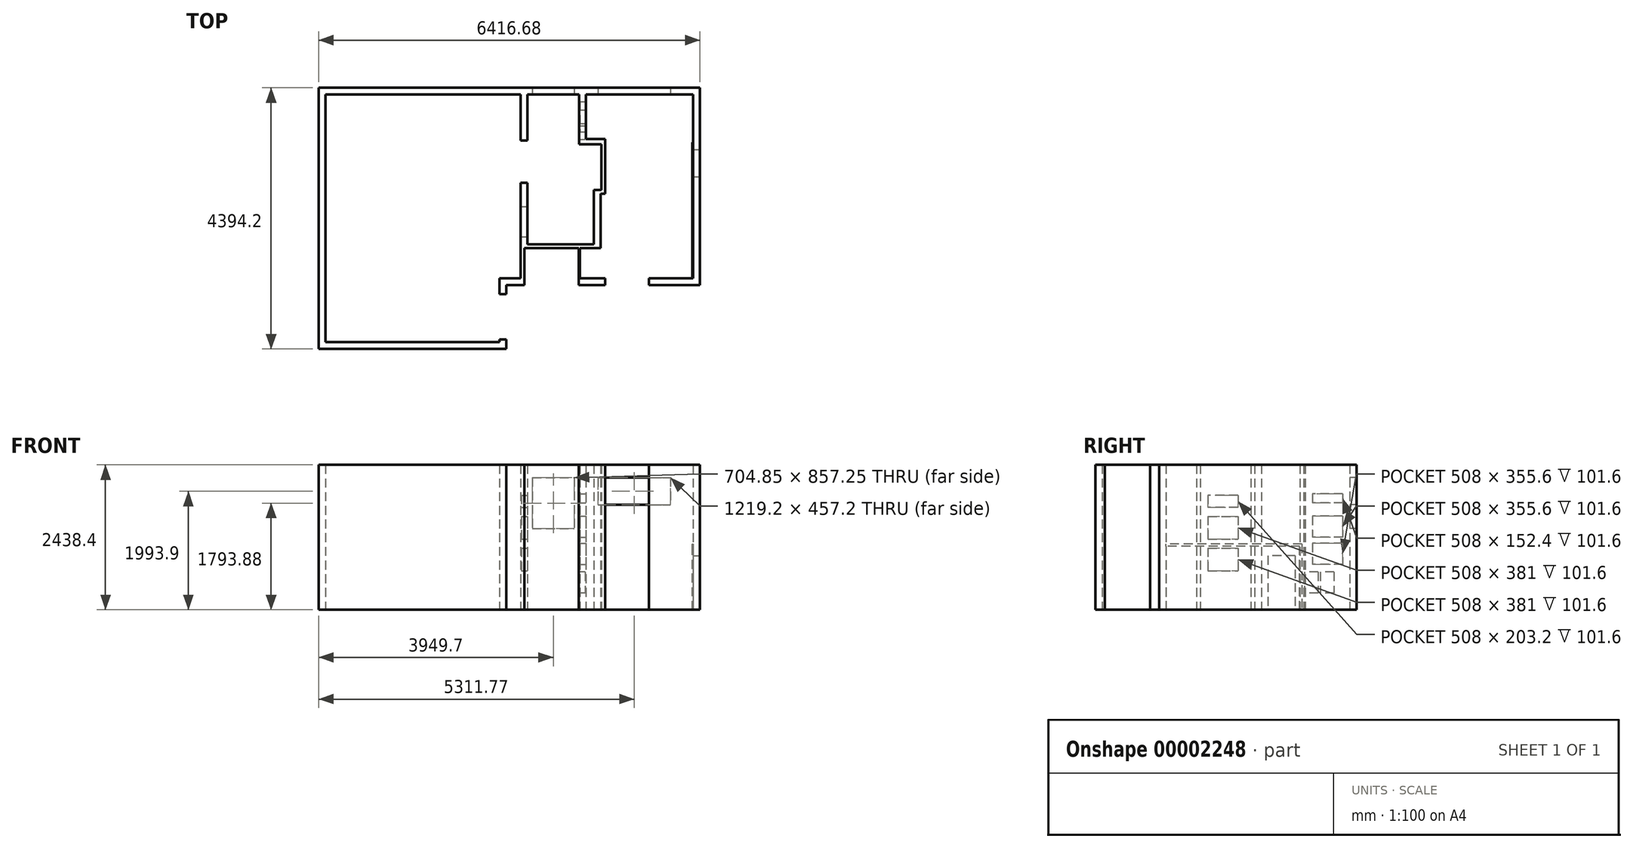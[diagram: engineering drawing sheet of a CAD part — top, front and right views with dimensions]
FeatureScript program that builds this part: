
annotation { "Feature Type Name" : "Feature", "Feature Type Description" : "" }
export const myFeature = defineFeature(function(context is Context, id is Id, definition is map)
    precondition{}
    {
        {
            var Q0;
            Q0=qCreatedBy(makeId("Top.planeOp"),FACE);
            var sketch = newSketch(context, id + "F0", { "sketchPlane" : qUnion([Q0])});
            skLineSegment(sketch, "E0.bottom", {"start": v(0, 0) * mm, "end": v(3286.13, 0) * mm});
            skLineSegment(sketch, "E0.top", {"start": v(0, -4165.6) * mm, "end": v(2930.53, -4165.6) * mm});
            skLineSegment(sketch, "E0.left", {"start": v(0, -4165.6) * mm, "end": v(0, 0) * mm});
            skLineSegment(sketch, "E0.right", {"start": v(2930.53, -3359.15) * mm, "end": v(2930.53, -3092.45) * mm});
            skLineSegment(sketch, "E1.bottom", {"start": v(2930.53, -3092.45) * mm, "end": v(3832.23, -3092.45) * mm});
            skLineSegment(sketch, "E1.right", {"start": v(3832.23, -3092.45) * mm, "end": v(3832.23, -1892.3) * mm});
            skLineSegment(sketch, "E2.top", {"start": v(3286.13, -1892.3) * mm, "end": v(3832.23, -1892.3) * mm});
            skLineSegment(sketch, "E2.right", {"start": v(3286.13, 0) * mm, "end": v(3286.13, -774.7) * mm});
            skLineSegment(sketch, "E3.0", {"start": v(-114.3, -4279.9) * mm, "end": v(3044.83, -4279.9) * mm});
            skLineSegment(sketch, "E3.1", {"start": v(-114.3, -4279.9) * mm, "end": v(-114.3, 114.3) * mm});
            skLineSegment(sketch, "E3.2", {"start": v(-114.3, 114.3) * mm, "end": v(3400.43, 114.3) * mm});
            skLineSegment(sketch, "E3.3", {"start": v(3400.43, 0) * mm, "end": v(3400.43, -774.7) * mm});
            skLineSegment(sketch, "E3.4", {"start": v(3400.43, -1778) * mm, "end": v(4422.78, -1778) * mm});
            skLineSegment(sketch, "E3.5", {"start": v(3044.83, -4279.9) * mm, "end": v(3044.83, -4121.15) * mm});
            skLineSegment(sketch, "E3.6", {"start": v(3946.53, -3092.45) * mm, "end": v(3946.53, -1892.3) * mm});
            skLineSegment(sketch, "E3.7", {"start": v(3044.83, -3206.75) * mm, "end": v(4594.23, -3206.75) * mm});
            skLineSegment(sketch, "E4", {"start": v(3400.43, 0) * mm, "end": v(4422.78, 0) * mm});
            skLineSegment(sketch, "E5", {"start": v(4422.78, 0) * mm, "end": v(4422.78, -1778) * mm});
            skLineSegment(sketch, "E6.0", {"start": v(4537.08, 0) * mm, "end": v(4537.08, -1892.3) * mm});
            skLineSegment(sketch, "E6.1", {"start": v(3400.43, 114.3) * mm, "end": v(4537.08, 114.3) * mm});
            skLineSegment(sketch, "E7.trimOffspring", {"start": v(3946.53, -1892.3) * mm, "end": v(4537.08, -1892.3) * mm});
            skLineSegment(sketch, "E8", {"start": v(4537.08, 114.3) * mm, "end": v(6302.38, 114.3) * mm});
            skLineSegment(sketch, "E9", {"start": v(6188.08, 0) * mm, "end": v(6188.08, -787.4) * mm});
            skLineSegment(sketch, "E10", {"start": v(6188.08, -787.4) * mm, "end": v(5400.68, -787.4) * mm});
            skLineSegment(sketch, "E11", {"start": v(5400.68, -787.4) * mm, "end": v(5400.68, -901.7) * mm});
            skLineSegment(sketch, "E12", {"start": v(5400.68, -901.7) * mm, "end": v(6188.08, -901.7) * mm});
            skLineSegment(sketch, "E13", {"start": v(6188.08, -901.7) * mm, "end": v(6188.08, -3092.45) * mm});
            skLineSegment(sketch, "E14", {"start": v(6302.38, -3206.75) * mm, "end": v(6302.38, 114.3) * mm});
            skLineSegment(sketch, "E15.trimOffspring", {"start": v(3946.53, -3092.45) * mm, "end": v(4594.23, -3092.45) * mm});
            skLineSegment(sketch, "E16.trimOffspring", {"start": v(4537.08, 0) * mm, "end": v(6188.08, 0) * mm});
            skLineSegment(sketch, "E17", {"start": v(3286.12, -774.7) * mm, "end": v(3400.43, -774.7) * mm});
            skLineSegment(sketch, "E18", {"start": v(3286.13, -1485.9) * mm, "end": v(3400.43, -1485.9) * mm});
            skLineSegment(sketch, "E19", {"start": v(4594.23, -3092.45) * mm, "end": v(4594.23, -3206.75) * mm});
            skLineSegment(sketch, "E20", {"start": v(5305.43, -3092.45) * mm, "end": v(5305.43, -3206.75) * mm});
            skLineSegment(sketch, "E21.trimOffspring", {"start": v(5305.43, -3092.45) * mm, "end": v(6188.08, -3092.45) * mm});
            skLineSegment(sketch, "E22.trimOffspring", {"start": v(5305.43, -3206.75) * mm, "end": v(6302.38, -3206.75) * mm});
            skLineSegment(sketch, "E23.trimOffspring", {"start": v(3286.13, -1485.9) * mm, "end": v(3286.13, -1892.3) * mm});
            skLineSegment(sketch, "E24.trimOffspring", {"start": v(3400.43, -1485.9) * mm, "end": v(3400.43, -1778) * mm});
            skLineSegment(sketch, "E25", {"start": v(2930.53, -3359.15) * mm, "end": v(3044.83, -3359.15) * mm});
            skLineSegment(sketch, "E26", {"start": v(2930.53, -4121.15) * mm, "end": v(3044.83, -4121.15) * mm});
            skLineSegment(sketch, "E27.trimOffspring", {"start": v(2930.53, -4121.15) * mm, "end": v(2930.53, -4165.6) * mm});
            skLineSegment(sketch, "E28.trimOffspring", {"start": v(3044.83, -3359.15) * mm, "end": v(3044.83, -3206.75) * mm});
            skSolve(sketch);
        }
        {
            var Q0;
            Q0=qCreatedBy(makeId("Top.planeOp"),FACE);
            var sketch = newSketch(context, id + "F1", { "sketchPlane" : qUnion([Q0])});
            skLineSegment(sketch, "E29.0", {"start": v(0, 0) * mm, "end": v(3286.13, 0) * mm});
            skLineSegment(sketch, "E29.1", {"start": v(0, -4165.6) * mm, "end": v(2930.53, -4165.6) * mm});
            skLineSegment(sketch, "E29.2", {"start": v(0, -4165.6) * mm, "end": v(0, 0) * mm});
            skLineSegment(sketch, "E29.3", {"start": v(2930.53, -3359.15) * mm, "end": v(2930.53, -3092.45) * mm});
            skLineSegment(sketch, "E29.4", {"start": v(2930.53, -3092.45) * mm, "end": v(3286.13, -3092.45) * mm});
            skLineSegment(sketch, "E29.7", {"start": v(3286.13, 0) * mm, "end": v(3286.13, -774.7) * mm});
            skLineSegment(sketch, "E29.8", {"start": v(-114.3, -4279.9) * mm, "end": v(3044.83, -4279.9) * mm});
            skLineSegment(sketch, "E29.9", {"start": v(-114.3, -4279.9) * mm, "end": v(-114.3, 114.3) * mm});
            skLineSegment(sketch, "E29.10", {"start": v(-114.3, 114.3) * mm, "end": v(3400.43, 114.3) * mm});
            skLineSegment(sketch, "E29.11", {"start": v(3400.43, 0) * mm, "end": v(3400.43, -774.7) * mm});
            skLineSegment(sketch, "E29.13", {"start": v(3044.83, -4279.9) * mm, "end": v(3044.83, -4121.15) * mm});
            skLineSegment(sketch, "E29.15", {"start": v(3044.83, -3206.75) * mm, "end": v(3349.63, -3206.75) * mm});
            skLineSegment(sketch, "E29.16", {"start": v(3400.43, 0) * mm, "end": v(4270.38, 0) * mm});
            skLineSegment(sketch, "E29.19", {"start": v(3400.43, 114.3) * mm, "end": v(4537.08, 114.3) * mm});
            skLineSegment(sketch, "E29.21", {"start": v(4537.08, 114.3) * mm, "end": v(6302.38, 114.3) * mm});
            skLineSegment(sketch, "E29.22", {"start": v(6188.08, 0) * mm, "end": v(6188.08, -917.58) * mm});
            skLineSegment(sketch, "E29.27", {"start": v(6302.38, -3206.75) * mm, "end": v(6302.38, 114.3) * mm});
            skLineSegment(sketch, "E29.29", {"start": v(4384.68, 0) * mm, "end": v(6188.08, 0) * mm});
            skLineSegment(sketch, "E29.30", {"start": v(3286.12, -774.7) * mm, "end": v(3400.43, -774.7) * mm});
            skLineSegment(sketch, "E29.31", {"start": v(3286.13, -1485.9) * mm, "end": v(3400.43, -1485.9) * mm});
            skLineSegment(sketch, "E29.34", {"start": v(5445.13, -3092.45) * mm, "end": v(6188.08, -3092.45) * mm});
            skLineSegment(sketch, "E29.35", {"start": v(5445.13, -3206.75) * mm, "end": v(6302.38, -3206.75) * mm});
            skLineSegment(sketch, "E29.36", {"start": v(3286.13, -1485.9) * mm, "end": v(3286.13, -1892.3) * mm});
            skLineSegment(sketch, "E29.37", {"start": v(3400.43, -1485.9) * mm, "end": v(3400.43, -1778) * mm});
            skLineSegment(sketch, "E29.38", {"start": v(2930.53, -3359.15) * mm, "end": v(3044.83, -3359.15) * mm});
            skLineSegment(sketch, "E29.39", {"start": v(2930.53, -4121.15) * mm, "end": v(3044.83, -4121.15) * mm});
            skLineSegment(sketch, "E29.40", {"start": v(2930.53, -4121.15) * mm, "end": v(2930.53, -4165.6) * mm});
            skLineSegment(sketch, "E29.41", {"start": v(3044.83, -3359.15) * mm, "end": v(3044.83, -3206.75) * mm});
            skLineSegment(sketch, "E30", {"start": v(3286.13, -1892.3) * mm, "end": v(3286.13, -3092.45) * mm});
            skPoint(sketch, "E31.start.orphan", {"position": v(3400.43, -1778) * mm});
            skLineSegment(sketch, "E32", {"start": v(3400.43, -1778) * mm, "end": v(3400.43, -2517.78) * mm});
            skLineSegment(sketch, "E33", {"start": v(4384.68, 0) * mm, "end": v(4384.68, -749.3) * mm});
            skLineSegment(sketch, "E34", {"start": v(4384.68, -749.3) * mm, "end": v(4708.53, -749.3) * mm});
            skLineSegment(sketch, "E35", {"start": v(4708.53, -749.3) * mm, "end": v(4708.53, -1666.87) * mm});
            skLineSegment(sketch, "E36.0", {"start": v(4645.03, -838.2) * mm, "end": v(4645.03, -1603.37) * mm});
            skLineSegment(sketch, "E36.1", {"start": v(4270.38, -838.2) * mm, "end": v(4645.03, -838.2) * mm});
            skLineSegment(sketch, "E36.2", {"start": v(4270.38, 0) * mm, "end": v(4270.38, -838.2) * mm});
            skLineSegment(sketch, "E37", {"start": v(5445.13, -3092.45) * mm, "end": v(5445.13, -3206.75) * mm});
            skLineSegment(sketch, "E38", {"start": v(4708.53, -3092.45) * mm, "end": v(4708.53, -3206.75) * mm});
            skLineSegment(sketch, "E39.bottom", {"start": v(5654.68, -1543.05) * mm, "end": v(6188.08, -1543.05) * mm, "construction": true});
            skLineSegment(sketch, "E39.left", {"start": v(5654.68, -1543.05) * mm, "end": v(5654.68, -3092.45) * mm, "construction": true});
            skLineSegment(sketch, "E39.right", {"start": v(6188.08, -1543.05) * mm, "end": v(6188.08, -2711.45) * mm, "construction": true});
            skLineSegment(sketch, "E40.bottom", {"start": v(4384.68, 0) * mm, "end": v(6188.08, 0) * mm, "construction": true});
            skLineSegment(sketch, "E40.top", {"start": v(4384.68, -749.3) * mm, "end": v(6188.08, -749.3) * mm, "construction": true});
            skLineSegment(sketch, "E40.left", {"start": v(4384.68, 0) * mm, "end": v(4384.68, -749.3) * mm, "construction": true});
            skLineSegment(sketch, "E40.right", {"start": v(6188.08, 0) * mm, "end": v(6188.08, -749.3) * mm, "construction": true});
            skLineSegment(sketch, "E41.0", {"start": v(4587.88, -647.7) * mm, "end": v(5984.88, -647.7) * mm, "construction": true});
            skLineSegment(sketch, "E41.1", {"start": v(4486.28, -203.2) * mm, "end": v(4486.28, -546.1) * mm, "construction": true});
            skLineSegment(sketch, "E41.2", {"start": v(4587.88, -101.6) * mm, "end": v(5984.88, -101.6) * mm, "construction": true});
            skLineSegment(sketch, "E41.3", {"start": v(6086.48, -203.2) * mm, "end": v(6086.48, -546.1) * mm, "construction": true});
            skPoint(sketch, "E42.visualSharp", {"position": v(4486.28, -101.6) * mm});
            skArc(sketch, "E42.filletArc", {"start": v(4587.88, -101.6) * mm, "mid": v(4516.03, -131.36) * mm, "end": v(4486.28, -203.2) * mm, "construction": true});
            skPoint(sketch, "E43.visualSharp", {"position": v(4486.28, -647.7) * mm});
            skArc(sketch, "E43.filletArc", {"start": v(4486.28, -546.1) * mm, "mid": v(4516.03, -617.94) * mm, "end": v(4587.88, -647.7) * mm, "construction": true});
            skPoint(sketch, "E44.visualSharp", {"position": v(6086.48, -647.7) * mm});
            skArc(sketch, "E44.filletArc", {"start": v(5984.88, -647.7) * mm, "mid": v(6056.72, -617.94) * mm, "end": v(6086.48, -546.1) * mm, "construction": true});
            skPoint(sketch, "E45.visualSharp", {"position": v(6086.48, -101.6) * mm});
            skArc(sketch, "E45.filletArc", {"start": v(6086.48, -203.2) * mm, "mid": v(6056.72, -131.36) * mm, "end": v(5984.88, -101.6) * mm, "construction": true});
            skLineSegment(sketch, "E46", {"start": v(3400.43, -2517.78) * mm, "end": v(4518.03, -2517.78) * mm});
            skLineSegment(sketch, "E47", {"start": v(3349.63, -3092.45) * mm, "end": v(3349.63, -3206.75) * mm});
            skLineSegment(sketch, "E48.trimOffspring", {"start": v(3349.63, -2581.27) * mm, "end": v(4264.03, -2581.27) * mm});
            skLineSegment(sketch, "E49", {"start": v(3400.43, -1603.37) * mm, "end": v(4645.03, -1603.37) * mm, "construction": true});
            skLineSegment(sketch, "E50", {"start": v(3349.63, -2581.27) * mm, "end": v(3349.63, -3092.45) * mm});
            skLineSegment(sketch, "E51", {"start": v(4264.03, -2581.27) * mm, "end": v(4264.03, -3206.75) * mm});
            skLineSegment(sketch, "E52", {"start": v(4283.08, -2581.27) * mm, "end": v(4283.08, -3092.45) * mm});
            skLineSegment(sketch, "E53.trimOffspring", {"start": v(4283.08, -3092.45) * mm, "end": v(4708.53, -3092.45) * mm});
            skLineSegment(sketch, "E54.trimOffspring", {"start": v(4264.03, -3206.75) * mm, "end": v(4708.53, -3206.75) * mm});
            skLineSegment(sketch, "E55", {"start": v(4111.63, -838.2) * mm, "end": v(4111.63, -1603.37) * mm, "construction": true});
            skLineSegment(sketch, "E56", {"start": v(4111.63, -838.2) * mm, "end": v(4270.38, -838.2) * mm, "construction": true});
            skLineSegment(sketch, "E57.trimOffspring", {"start": v(4283.08, -2581.27) * mm, "end": v(4632.33, -2581.27) * mm});
            skLineSegment(sketch, "E58.bottom", {"start": v(5816.21, -1708.15) * mm, "end": v(5968.61, -1708.15) * mm, "construction": true});
            skLineSegment(sketch, "E58.top", {"start": v(5816.21, -2012.95) * mm, "end": v(5968.61, -2012.95) * mm, "construction": true});
            skLineSegment(sketch, "E58.left", {"start": v(5765.41, -1758.95) * mm, "end": v(5765.41, -1962.15) * mm, "construction": true});
            skLineSegment(sketch, "E58.right", {"start": v(6019.41, -1758.95) * mm, "end": v(6019.41, -1962.15) * mm, "construction": true});
            skLineSegment(sketch, "E59", {"start": v(5654.68, -2317.75) * mm, "end": v(5806.28, -2317.75) * mm, "construction": true});
            skPoint(sketch, "E60.visualSharp", {"position": v(5765.41, -1708.15) * mm});
            skArc(sketch, "E60.filletArc", {"start": v(5816.21, -1708.15) * mm, "mid": v(5780.3, -1723.03) * mm, "end": v(5765.41, -1758.95) * mm, "construction": true});
            skPoint(sketch, "E61.visualSharp", {"position": v(6019.41, -1708.15) * mm});
            skArc(sketch, "E61.filletArc", {"start": v(6019.41, -1758.95) * mm, "mid": v(6004.54, -1723.03) * mm, "end": v(5968.61, -1708.15) * mm, "construction": true});
            skPoint(sketch, "E62.visualSharp", {"position": v(6019.41, -2012.95) * mm});
            skArc(sketch, "E62.filletArc", {"start": v(5968.61, -2012.95) * mm, "mid": v(6004.54, -1998.07) * mm, "end": v(6019.41, -1962.15) * mm, "construction": true});
            skPoint(sketch, "E63.visualSharp", {"position": v(5765.41, -2012.95) * mm});
            skArc(sketch, "E63.filletArc", {"start": v(5765.41, -1962.15) * mm, "mid": v(5780.3, -1998.07) * mm, "end": v(5816.21, -2012.95) * mm, "construction": true});
            skLineSegment(sketch, "E64.0.MirrorCS", {"start": v(6019.41, -2876.55) * mm, "end": v(6019.41, -2673.35) * mm, "construction": true});
            skArc(sketch, "E64.1.MirrorCS", {"start": v(6019.41, -2876.55) * mm, "mid": v(6004.54, -2912.47) * mm, "end": v(5968.61, -2927.35) * mm, "construction": true});
            skLineSegment(sketch, "E64.2.MirrorCS", {"start": v(5816.21, -2927.35) * mm, "end": v(5968.61, -2927.35) * mm, "construction": true});
            skPoint(sketch, "E64.3.MirrorP", {"position": v(5765.41, -2622.55) * mm});
            skPoint(sketch, "E64.4.MirrorP", {"position": v(6019.41, -2927.35) * mm});
            skArc(sketch, "E64.5.MirrorCS", {"start": v(5816.21, -2927.35) * mm, "mid": v(5780.3, -2912.47) * mm, "end": v(5765.41, -2876.55) * mm, "construction": true});
            skPoint(sketch, "E64.6.MirrorP", {"position": v(6019.41, -2622.55) * mm});
            skLineSegment(sketch, "E64.7.MirrorCS", {"start": v(5816.21, -2622.55) * mm, "end": v(5968.61, -2622.55) * mm, "construction": true});
            skArc(sketch, "E64.8.MirrorCS", {"start": v(5968.61, -2622.55) * mm, "mid": v(6004.54, -2637.43) * mm, "end": v(6019.41, -2673.35) * mm, "construction": true});
            skPoint(sketch, "E64.9.MirrorP", {"position": v(5765.41, -2927.35) * mm});
            skLineSegment(sketch, "E64.10.MirrorCS", {"start": v(5765.41, -2876.55) * mm, "end": v(5765.41, -2673.35) * mm, "construction": true});
            skArc(sketch, "E64.11.MirrorCS", {"start": v(5765.41, -2673.35) * mm, "mid": v(5780.3, -2637.43) * mm, "end": v(5816.21, -2622.55) * mm, "construction": true});
            skLineSegment(sketch, "E65", {"start": v(5765.41, -1860.55) * mm, "end": v(6019.41, -1860.55) * mm, "construction": true});
            skLineSegment(sketch, "E66", {"start": v(4645.03, -1603.37) * mm, "end": v(4518.03, -1603.37) * mm});
            skLineSegment(sketch, "E67", {"start": v(4518.03, -1603.37) * mm, "end": v(4518.03, -2517.78) * mm});
            skLineSegment(sketch, "E68", {"start": v(4708.53, -1666.87) * mm, "end": v(4632.33, -1666.87) * mm});
            skLineSegment(sketch, "E69", {"start": v(4632.33, -1666.87) * mm, "end": v(4632.33, -2581.27) * mm});
            skPoint(sketch, "E70.orphan", {"position": v(4708.53, -2581.27) * mm});
            skLineSegment(sketch, "E71.trimOffspring", {"start": v(6188.08, -917.58) * mm, "end": v(6188.08, -3092.45) * mm});
            skLineSegment(sketch, "E72", {"start": v(6188.08, -749.3) * mm, "end": v(6188.08, -1543.05) * mm, "construction": true});
            skLineSegment(sketch, "E73", {"start": v(6188.08, -1146.18) * mm, "end": v(6289.68, -1146.18) * mm, "construction": true});
            skSolve(sketch);
        }
        {
            var Q0;
            Q0 = qSketchRegion(id + "F1", true);
            extrude(context, id + "F2", {"entities" : qUnion([Q0]), "depth" : 2438.4 * mm});
        }
        {
            var Q0;
            Q0=makeQuery(id+"F2.opExtrude","SWEPT_FACE",FACE,{"disambiguationData":[OSD([sQuery(id+"F1.wireOp",EDGE,"E29.16")])]});
            var sketch = newSketch(context, id + "F3", { "sketchPlane" : qUnion([Q0])});
            skLineSegment(sketch, "E74.bottom", {"start": v(3482.98, 2222.5) * mm, "end": v(4187.83, 2222.5) * mm});
            skLineSegment(sketch, "E74.top", {"start": v(3482.98, 1365.25) * mm, "end": v(4187.83, 1365.25) * mm});
            skLineSegment(sketch, "E74.left", {"start": v(3482.98, 2222.5) * mm, "end": v(3482.98, 1365.25) * mm});
            skLineSegment(sketch, "E74.right", {"start": v(4187.83, 2222.5) * mm, "end": v(4187.83, 1365.25) * mm});
            skLineSegment(sketch, "E75", {"start": v(3835.4, 2438.4) * mm, "end": v(3835.4, 2222.5) * mm, "construction": true});
            skSolve(sketch);
        }
        {
            var Q0;
            Q0=makeQuery(id+"F3.imprint","IMPRINT",FACE,{"disambiguationData":[TD([[makeQuery(id+"F3.imprint","IMPRINT",EDGE,{"derivedFrom":sQuery(id+"F3.wireOp",EDGE,"E74.bottom")}),-1.0]])]});
            extrude(context, id + "F4", {"entities" : qUnion([Q0]), "operationType" : NewBodyOperationType.REMOVE, "endBound" : BoundingType.UP_TO_NEXT, "oppositeDirection" : true, "depth" : 25.4 * mm});
        }
        {
            var Q0;
            Q0=makeQuery(id+"F2.opExtrude","SWEPT_FACE",FACE,{"disambiguationData":[OSD([sQuery(id+"F1.wireOp",EDGE,"E29.29")])]});
            var sketch = newSketch(context, id + "F5", { "sketchPlane" : qUnion([Q0])});
            skLineSegment(sketch, "E76.bottom", {"start": v(4587.88, 2222.5) * mm, "end": v(5807.08, 2222.5) * mm});
            skLineSegment(sketch, "E76.top", {"start": v(4587.88, 1765.3) * mm, "end": v(5807.08, 1765.3) * mm});
            skLineSegment(sketch, "E76.left", {"start": v(4587.88, 2222.5) * mm, "end": v(4587.88, 1765.3) * mm});
            skLineSegment(sketch, "E76.right", {"start": v(5807.08, 2222.5) * mm, "end": v(5807.08, 1765.3) * mm});
            skSolve(sketch);
        }
        {
            var Q0;
            Q0=makeQuery(id+"F5.imprint","IMPRINT",FACE,{"disambiguationData":[TD([[makeQuery(id+"F5.imprint","IMPRINT",EDGE,{"derivedFrom":sQuery(id+"F5.wireOp",EDGE,"E76.bottom")}),-1.0]])]});
            extrude(context, id + "F6", {"entities" : qUnion([Q0]), "operationType" : NewBodyOperationType.REMOVE, "endBound" : BoundingType.UP_TO_NEXT, "oppositeDirection" : true, "depth" : 25.4 * mm});
        }
        {
            var Q0;
            Q0=qCreatedBy(makeId("Top.planeOp"),FACE);
            var sketch = newSketch(context, id + "F7", { "sketchPlane" : qUnion([Q0])});
            skCircle(sketch, "E77", {"center": v(3835.4, -304.8) * mm, "radius": 50.8 * mm});
            skLineSegment(sketch, "E78.0", {"start": v(3400.43, 0) * mm, "end": v(4270.38, 0) * mm, "construction": true});
            skLineSegment(sketch, "E79", {"start": v(3835.4, 0) * mm, "end": v(3835.4, -304.8) * mm, "construction": true});
            skLineSegment(sketch, "E80.0", {"start": v(6188.08, 0) * mm, "end": v(6188.08, 0) * mm});
            skLineSegment(sketch, "E81", {"start": v(6188.08, -381) * mm, "end": v(6010.28, -381) * mm, "construction": true});
            skLineSegment(sketch, "E82", {"start": v(6289.68, -1152.53) * mm, "end": v(6035.68, -1152.53) * mm, "construction": true});
            skCircle(sketch, "E83", {"center": v(6035.68, -1152.53) * mm, "radius": 50.8 * mm, "construction": true});
            skLineSegment(sketch, "E84", {"start": v(6243.87, -987.43) * mm, "end": v(6049.67, -987.43) * mm});
            skCircle(sketch, "E85", {"center": v(6236.76, -381) * mm, "radius": 25.4 * mm});
            skCircle(sketch, "E86", {"center": v(6229.2, -322.77) * mm, "radius": 6.35 * mm});
            skCircle(sketch, "E87", {"center": v(6236.76, -446.63) * mm, "radius": 6.35 * mm});
            skCircle(sketch, "E88", {"center": v(6243.87, -987.43) * mm, "radius": 6.35 * mm});
            skCircle(sketch, "E89", {"center": v(6230.05, -1873.25) * mm, "radius": 25.4 * mm});
            skCircle(sketch, "E90", {"center": v(6230.05, -2787.65) * mm, "radius": 25.4 * mm});
            skLineSegment(sketch, "E91", {"start": v(6230.05, -2787.65) * mm, "end": v(5900.55, -2787.65) * mm, "construction": true});
            skLineSegment(sketch, "E92", {"start": v(6230.05, -1873.25) * mm, "end": v(5904.91, -1873.25) * mm, "construction": true});
            skCircle(sketch, "E93", {"center": v(4729.13, -1092.2) * mm, "radius": 25.4 * mm});
            skLineSegment(sketch, "E94", {"start": v(4729.13, -1092.2) * mm, "end": v(4320.88, -1092.2) * mm, "construction": true});
            skCircle(sketch, "E95", {"center": v(4467.23, -2111.38) * mm, "radius": 25.4 * mm});
            skLineSegment(sketch, "E96", {"start": v(4467.23, -2111.38) * mm, "end": v(4717.47, -2111.38) * mm, "construction": true});
            skCircle(sketch, "E97", {"center": v(6010.28, -381) * mm, "radius": 25.4 * mm});
            skLineSegment(sketch, "E98", {"start": v(6230.05, -1873.25) * mm, "end": v(6230.05, -2787.65) * mm, "construction": true});
            skCircle(sketch, "E99", {"center": v(6230.05, -2330.45) * mm, "radius": 25.4 * mm});
            skLineSegment(sketch, "E100", {"start": v(6230.05, -2330.45) * mm, "end": v(5792.73, -2330.45) * mm, "construction": true});
            skLineSegment(sketch, "E101", {"start": v(4003, 0) * mm, "end": v(4003, -124.8) * mm, "construction": true});
            skLineSegment(sketch, "E102", {"start": v(4670.25, -988.92) * mm, "end": v(4576.26, -988.92) * mm, "construction": true});
            skLineSegment(sketch, "E103", {"start": v(4670.25, -1173.93) * mm, "end": v(4579.42, -1173.93) * mm, "construction": true});
            skSolve(sketch);
        }
        {
            var Q0;
            Q0=makeQuery(id+"F2.opExtrude","SWEPT_FACE",FACE,{"disambiguationData":[OSD([sQuery(id+"F1.wireOp",EDGE,"E33")])]});
            var sketch = newSketch(context, id + "F8", { "sketchPlane" : qUnion([Q0])});
            skLineSegment(sketch, "E104.bottom", {"start": v(-120.65, 1952.83) * mm, "end": v(-628.65, 1952.83) * mm});
            skLineSegment(sketch, "E104.top", {"start": v(-120.65, 1800.43) * mm, "end": v(-628.65, 1800.43) * mm});
            skLineSegment(sketch, "E104.left", {"start": v(-120.65, 1952.83) * mm, "end": v(-120.65, 1800.43) * mm});
            skLineSegment(sketch, "E104.right", {"start": v(-628.65, 1952.83) * mm, "end": v(-628.65, 1800.43) * mm});
            skLineSegment(sketch, "E105.bottom", {"start": v(-120.65, 1574.8) * mm, "end": v(-628.65, 1574.8) * mm});
            skLineSegment(sketch, "E105.top", {"start": v(-120.65, 1219.2) * mm, "end": v(-628.65, 1219.2) * mm});
            skLineSegment(sketch, "E105.left", {"start": v(-120.65, 1574.8) * mm, "end": v(-120.65, 1219.2) * mm});
            skLineSegment(sketch, "E105.right", {"start": v(-628.65, 1574.8) * mm, "end": v(-628.65, 1219.2) * mm});
            skLineSegment(sketch, "E106.bottom", {"start": v(-120.65, 762) * mm, "end": v(-628.65, 762) * mm});
            skLineSegment(sketch, "E106.top", {"start": v(-120.65, 1117.6) * mm, "end": v(-628.65, 1117.6) * mm});
            skLineSegment(sketch, "E106.left", {"start": v(-120.65, 1117.6) * mm, "end": v(-120.65, 762) * mm});
            skLineSegment(sketch, "E106.right", {"start": v(-628.65, 1117.6) * mm, "end": v(-628.65, 762) * mm});
            skLineSegment(sketch, "E107", {"start": v(-374.65, 1800.43) * mm, "end": v(-374.65, 1574.8) * mm, "construction": true});
            skLineSegment(sketch, "E108", {"start": v(-374.65, 1219.2) * mm, "end": v(-374.65, 762) * mm, "construction": true});
            skLineSegment(sketch, "E109.0", {"start": v(0, 2438.4) * mm, "end": v(-749.3, 2438.4) * mm, "construction": true});
            skLineSegment(sketch, "E110", {"start": v(-374.65, 2438.4) * mm, "end": v(-374.65, 1800.43) * mm, "construction": true});
            skSolve(sketch);
        }
        {
            var Q0;
            {Q0=qUnion([makeQuery(id+"F8.imprint","IMPRINT",FACE,{"disambiguationData":[TD([[makeQuery(id+"F8.imprint","IMPRINT",EDGE,{"derivedFrom":sQuery(id+"F8.wireOp",EDGE,"E104.bottom")}),1.0]])]}),makeQuery(id+"F8.imprint","IMPRINT",FACE,{"disambiguationData":[TD([[makeQuery(id+"F8.imprint","IMPRINT",EDGE,{"derivedFrom":sQuery(id+"F8.wireOp",EDGE,"E105.bottom")}),1.0]])]}),makeQuery(id+"F8.imprint","IMPRINT",FACE,{"disambiguationData":[TD([[makeQuery(id+"F8.imprint","IMPRINT",EDGE,{"derivedFrom":sQuery(id+"F8.wireOp",EDGE,"E106.bottom")}),-1.0]])]})]);}
            extrude(context, id + "F9", {"entities" : qUnion([Q0]), "operationType" : NewBodyOperationType.REMOVE, "oppositeDirection" : true, "depth" : 101.6 * mm});
        }
        {
            var Q0;
            Q0=makeQuery(id+"F2.opExtrude","SWEPT_FACE",FACE,{"disambiguationData":[OSD([sQuery(id+"F1.wireOp",EDGE,"E36.2")])]});
            var sketch = newSketch(context, id + "F10", { "sketchPlane" : qUnion([Q0])});
            skLineSegment(sketch, "E111.bottom", {"start": v(266.7, 635) * mm, "end": v(495.3, 635) * mm});
            skLineSegment(sketch, "E111.top", {"start": v(266.7, 279.4) * mm, "end": v(495.3, 279.4) * mm});
            skLineSegment(sketch, "E111.left", {"start": v(266.7, 635) * mm, "end": v(266.7, 279.4) * mm});
            skLineSegment(sketch, "E111.right", {"start": v(495.3, 635) * mm, "end": v(495.3, 279.4) * mm});
            skLineSegment(sketch, "E112.0", {"start": v(0, 2438.4) * mm, "end": v(838.2, 2438.4) * mm, "construction": true});
            skLineSegment(sketch, "E113.bottom", {"start": v(533.4, 635) * mm, "end": v(762, 635) * mm});
            skLineSegment(sketch, "E113.top", {"start": v(533.4, 279.4) * mm, "end": v(762, 279.4) * mm});
            skLineSegment(sketch, "E113.left", {"start": v(533.4, 635) * mm, "end": v(533.4, 279.4) * mm});
            skLineSegment(sketch, "E113.right", {"start": v(762, 635) * mm, "end": v(762, 279.4) * mm});
            skSolve(sketch);
        }
        {
            var Q0;
            {Q0=qUnion([makeQuery(id+"F10.imprint","IMPRINT",FACE,{"disambiguationData":[TD([[makeQuery(id+"F10.imprint","IMPRINT",EDGE,{"derivedFrom":sQuery(id+"F10.wireOp",EDGE,"E111.bottom")}),-1.0]])]}),makeQuery(id+"F10.imprint","IMPRINT",FACE,{"disambiguationData":[TD([[makeQuery(id+"F10.imprint","IMPRINT",EDGE,{"derivedFrom":sQuery(id+"F10.wireOp",EDGE,"E113.bottom")}),-1.0]])]})]);}
            extrude(context, id + "F11", {"entities" : qUnion([Q0]), "operationType" : NewBodyOperationType.REMOVE, "oppositeDirection" : true, "depth" : 101.6 * mm});
        }
        {
            var Q0;
            Q0=makeQuery(id+"F2.opExtrude","SWEPT_FACE",FACE,{"disambiguationData":[OSD([sQuery(id+"F1.wireOp",EDGE,"E32")])]});
            var sketch = newSketch(context, id + "F12", { "sketchPlane" : qUnion([Q0])});
            skLineSegment(sketch, "E114.bottom", {"start": v(-2390.77, 1572.45) * mm, "end": v(-1882.77, 1572.45) * mm});
            skLineSegment(sketch, "E114.top", {"start": v(-2390.77, 1191.45) * mm, "end": v(-1882.77, 1191.45) * mm});
            skLineSegment(sketch, "E114.left", {"start": v(-2390.77, 1572.45) * mm, "end": v(-2390.77, 1191.45) * mm});
            skLineSegment(sketch, "E114.right", {"start": v(-1882.77, 1572.45) * mm, "end": v(-1882.77, 1191.45) * mm});
            skLineSegment(sketch, "E115.bottom", {"start": v(-2390.77, 1039.05) * mm, "end": v(-1882.77, 1039.05) * mm});
            skLineSegment(sketch, "E115.top", {"start": v(-2390.77, 658.05) * mm, "end": v(-1882.77, 658.05) * mm});
            skLineSegment(sketch, "E115.left", {"start": v(-2390.77, 1039.05) * mm, "end": v(-2390.77, 658.05) * mm});
            skLineSegment(sketch, "E115.right", {"start": v(-1882.77, 1039.05) * mm, "end": v(-1882.77, 658.05) * mm});
            skLineSegment(sketch, "E116.bottom", {"start": v(-1882.77, 1928.05) * mm, "end": v(-2390.77, 1928.05) * mm});
            skLineSegment(sketch, "E116.top", {"start": v(-1882.77, 1724.85) * mm, "end": v(-2390.77, 1724.85) * mm});
            skLineSegment(sketch, "E116.left", {"start": v(-1882.77, 1928.05) * mm, "end": v(-1882.77, 1724.85) * mm});
            skLineSegment(sketch, "E116.right", {"start": v(-2390.77, 1928.05) * mm, "end": v(-2390.77, 1724.85) * mm});
            skSolve(sketch);
        }
        {
            var Q0;
            {Q0=qUnion([makeQuery(id+"F12.imprint","IMPRINT",FACE,{"disambiguationData":[TD([[makeQuery(id+"F12.imprint","IMPRINT",EDGE,{"derivedFrom":sQuery(id+"F12.wireOp",EDGE,"E114.bottom")}),-1.0]])]}),makeQuery(id+"F12.imprint","IMPRINT",FACE,{"disambiguationData":[TD([[makeQuery(id+"F12.imprint","IMPRINT",EDGE,{"derivedFrom":sQuery(id+"F12.wireOp",EDGE,"E115.bottom")}),-1.0]])]}),makeQuery(id+"F12.imprint","IMPRINT",FACE,{"disambiguationData":[TD([[makeQuery(id+"F12.imprint","IMPRINT",EDGE,{"derivedFrom":sQuery(id+"F12.wireOp",EDGE,"E116.bottom")}),1.0]])]})]);}
            extrude(context, id + "F13", {"entities" : qUnion([Q0]), "operationType" : NewBodyOperationType.REMOVE, "oppositeDirection" : true, "depth" : 101.6 * mm});
        }
        {
            var Q0;
            Q0=makeQuery(id+"F2.opExtrude","CAP_FACE",FACE,{"disambiguationData":[OSD([sQuery(id+"F1.wireOp",EDGE,"E29.0"),sQuery(id+"F1.wireOp",EDGE,"E29.1"),sQuery(id+"F1.wireOp",EDGE,"E29.2"),sQuery(id+"F1.wireOp",EDGE,"E29.3"),sQuery(id+"F1.wireOp",EDGE,"E29.4"),sQuery(id+"F1.wireOp",EDGE,"E29.7"),sQuery(id+"F1.wireOp",EDGE,"E29.8"),sQuery(id+"F1.wireOp",EDGE,"E29.9"),sQuery(id+"F1.wireOp",EDGE,"E29.11"),sQuery(id+"F1.wireOp",EDGE,"E29.13"),sQuery(id+"F1.wireOp",EDGE,"E29.15"),sQuery(id+"F1.wireOp",EDGE,"E29.16"),sQuery(id+"F1.wireOp",EDGE,"E29.21"),sQuery(id+"F1.wireOp",EDGE,"E29.22"),sQuery(id+"F1.wireOp",EDGE,"E29.27"),sQuery(id+"F1.wireOp",EDGE,"E29.29"),sQuery(id+"F1.wireOp",EDGE,"E29.30"),sQuery(id+"F1.wireOp",EDGE,"E29.31"),sQuery(id+"F1.wireOp",EDGE,"E29.34"),sQuery(id+"F1.wireOp",EDGE,"E29.35"),sQuery(id+"F1.wireOp",EDGE,"E29.36"),sQuery(id+"F1.wireOp",EDGE,"E29.38"),sQuery(id+"F1.wireOp",EDGE,"E29.39"),sQuery(id+"F1.wireOp",EDGE,"E29.40"),sQuery(id+"F1.wireOp",EDGE,"E29.41"),sQuery(id+"F1.wireOp",EDGE,"E32"),sQuery(id+"F1.wireOp",EDGE,"E33"),sQuery(id+"F1.wireOp",EDGE,"E34"),sQuery(id+"F1.wireOp",EDGE,"E35"),sQuery(id+"F1.wireOp",EDGE,"E36.0"),sQuery(id+"F1.wireOp",EDGE,"E36.1"),sQuery(id+"F1.wireOp",EDGE,"E36.2"),sQuery(id+"F1.wireOp",EDGE,"E37"),sQuery(id+"F1.wireOp",EDGE,"E38"),sQuery(id+"F1.wireOp",EDGE,"E46"),sQuery(id+"F1.wireOp",EDGE,"E47"),sQuery(id+"F1.wireOp",EDGE,"E48.trimOffspring"),sQuery(id+"F1.wireOp",EDGE,"E51"),sQuery(id+"F1.wireOp",EDGE,"E52"),sQuery(id+"F1.wireOp",EDGE,"E53.trimOffspring"),sQuery(id+"F1.wireOp",EDGE,"E54.trimOffspring"),sQuery(id+"F1.wireOp",EDGE,"E57.trimOffspring"),sQuery(id+"F1.wireOp",EDGE,"E66"),sQuery(id+"F1.wireOp",EDGE,"E67"),sQuery(id+"F1.wireOp",EDGE,"E68"),sQuery(id+"F1.wireOp",EDGE,"E69")])],"isStart":true});
            var sketch = newSketch(context, id + "F14", { "sketchPlane" : qUnion([Q0])});
            skLineSegment(sketch, "E117.bottom", {"start": v(6188.08, 923.93) * mm, "end": v(6289.68, 923.93) * mm});
            skLineSegment(sketch, "E117.top", {"start": v(6188.08, 1381.13) * mm, "end": v(6289.68, 1381.13) * mm});
            skLineSegment(sketch, "E117.left", {"start": v(6188.08, 923.93) * mm, "end": v(6188.08, 1381.13) * mm});
            skLineSegment(sketch, "E117.right", {"start": v(6289.68, 923.93) * mm, "end": v(6289.68, 1381.13) * mm});
            skLineSegment(sketch, "E118", {"start": v(6289.68, 1152.53) * mm, "end": v(6188.08, 1152.53) * mm, "construction": true});
            skSolve(sketch);
        }
        {
            var Q0;
            Q0 = qSketchRegion(id + "F14", true);
            extrude(context, id + "F15", {"entities" : qUnion([Q0]), "operationType" : NewBodyOperationType.REMOVE, "oppositeDirection" : true, "depth" : 908.05 * mm});
        }
        {
            var Q0;
            Q0=makeQuery(id+"F2.opExtrude","SWEPT_FACE",FACE,{"disambiguationData":[OSD([sQuery(id+"F1.wireOp",EDGE,"E29.34")])]});
            var sketch = newSketch(context, id + "F16", { "sketchPlane" : qUnion([Q0])});
            skLineSegment(sketch, "E119", {"start": v(-6188.08, 1104.9) * mm, "end": v(-6188.08, 1066.8) * mm});
            skLineSegment(sketch, "E120", {"start": v(-6188.08, 1066.8) * mm, "end": v(-6177.01, 1066.8) * mm});
            skLineSegment(sketch, "E121", {"start": v(-6177.01, 1066.8) * mm, "end": v(-6177.01, 1104.9) * mm});
            skLineSegment(sketch, "E122", {"start": v(-6177.01, 1104.9) * mm, "end": v(-6188.08, 1104.9) * mm});
            skSolve(sketch);
        }
        {
            var Q0;
            Q0 = qSketchRegion(id + "F16", true);
            extrude(context, id + "F17", {"entities" : qUnion([Q0]), "operationType" : NewBodyOperationType.ADD, "depth" : 2286 * mm});
        }
        {
            var Q0;
            Q0=makeQuery(id+"F17.opExtrude","SWEPT_FACE",FACE,{"disambiguationData":[OSD([sQuery(id+"F16.wireOp",EDGE,"E122")])]});
            var sketch = newSketch(context, id + "F18", { "sketchPlane" : qUnion([Q0])});
            skLineSegment(sketch, "E123.bottom", {"start": v(6188.08, -806.45) * mm, "end": v(6177.01, -806.45) * mm});
            skLineSegment(sketch, "E123.top", {"start": v(6188.08, -844.55) * mm, "end": v(6177.01, -844.55) * mm});
            skLineSegment(sketch, "E123.left", {"start": v(6188.08, -806.45) * mm, "end": v(6188.08, -844.55) * mm});
            skLineSegment(sketch, "E123.right", {"start": v(6177.01, -806.45) * mm, "end": v(6177.01, -844.55) * mm});
            skSolve(sketch);
        }
        {
            var Q0;
            Q0 = qSketchRegion(id + "F18", true);
            var Q1;
            Q1=makeQuery(id+"F2.opExtrude","CAP_FACE",FACE,{"disambiguationData":[OSD([sQuery(id+"F1.wireOp",EDGE,"E29.0"),sQuery(id+"F1.wireOp",EDGE,"E29.1"),sQuery(id+"F1.wireOp",EDGE,"E29.2"),sQuery(id+"F1.wireOp",EDGE,"E29.3"),sQuery(id+"F1.wireOp",EDGE,"E29.4"),sQuery(id+"F1.wireOp",EDGE,"E29.7"),sQuery(id+"F1.wireOp",EDGE,"E29.8"),sQuery(id+"F1.wireOp",EDGE,"E29.9"),sQuery(id+"F1.wireOp",EDGE,"E29.11"),sQuery(id+"F1.wireOp",EDGE,"E29.13"),sQuery(id+"F1.wireOp",EDGE,"E29.15"),sQuery(id+"F1.wireOp",EDGE,"E29.16"),sQuery(id+"F1.wireOp",EDGE,"E29.21"),sQuery(id+"F1.wireOp",EDGE,"E29.22"),sQuery(id+"F1.wireOp",EDGE,"E29.27"),sQuery(id+"F1.wireOp",EDGE,"E29.29"),sQuery(id+"F1.wireOp",EDGE,"E29.30"),sQuery(id+"F1.wireOp",EDGE,"E29.31"),sQuery(id+"F1.wireOp",EDGE,"E29.34"),sQuery(id+"F1.wireOp",EDGE,"E29.35"),sQuery(id+"F1.wireOp",EDGE,"E29.36"),sQuery(id+"F1.wireOp",EDGE,"E29.38"),sQuery(id+"F1.wireOp",EDGE,"E29.39"),sQuery(id+"F1.wireOp",EDGE,"E29.40"),sQuery(id+"F1.wireOp",EDGE,"E29.41"),sQuery(id+"F1.wireOp",EDGE,"E32"),sQuery(id+"F1.wireOp",EDGE,"E33"),sQuery(id+"F1.wireOp",EDGE,"E34"),sQuery(id+"F1.wireOp",EDGE,"E35"),sQuery(id+"F1.wireOp",EDGE,"E36.0"),sQuery(id+"F1.wireOp",EDGE,"E36.1"),sQuery(id+"F1.wireOp",EDGE,"E36.2"),sQuery(id+"F1.wireOp",EDGE,"E37"),sQuery(id+"F1.wireOp",EDGE,"E38"),sQuery(id+"F1.wireOp",EDGE,"E46"),sQuery(id+"F1.wireOp",EDGE,"E47"),sQuery(id+"F1.wireOp",EDGE,"E48.trimOffspring"),sQuery(id+"F1.wireOp",EDGE,"E51"),sQuery(id+"F1.wireOp",EDGE,"E52"),sQuery(id+"F1.wireOp",EDGE,"E53.trimOffspring"),sQuery(id+"F1.wireOp",EDGE,"E54.trimOffspring"),sQuery(id+"F1.wireOp",EDGE,"E57.trimOffspring"),sQuery(id+"F1.wireOp",EDGE,"E66"),sQuery(id+"F1.wireOp",EDGE,"E67"),sQuery(id+"F1.wireOp",EDGE,"E68"),sQuery(id+"F1.wireOp",EDGE,"E69")])],"isStart":true});
            extrude(context, id + "F19", {"entities" : qUnion([Q0]), "operationType" : NewBodyOperationType.ADD, "endBound" : BoundingType.UP_TO_SURFACE, "oppositeDirection" : true, "endBoundEntityFace" : qUnion([Q1]), "depth" : 25.4 * mm});
        }
    });
